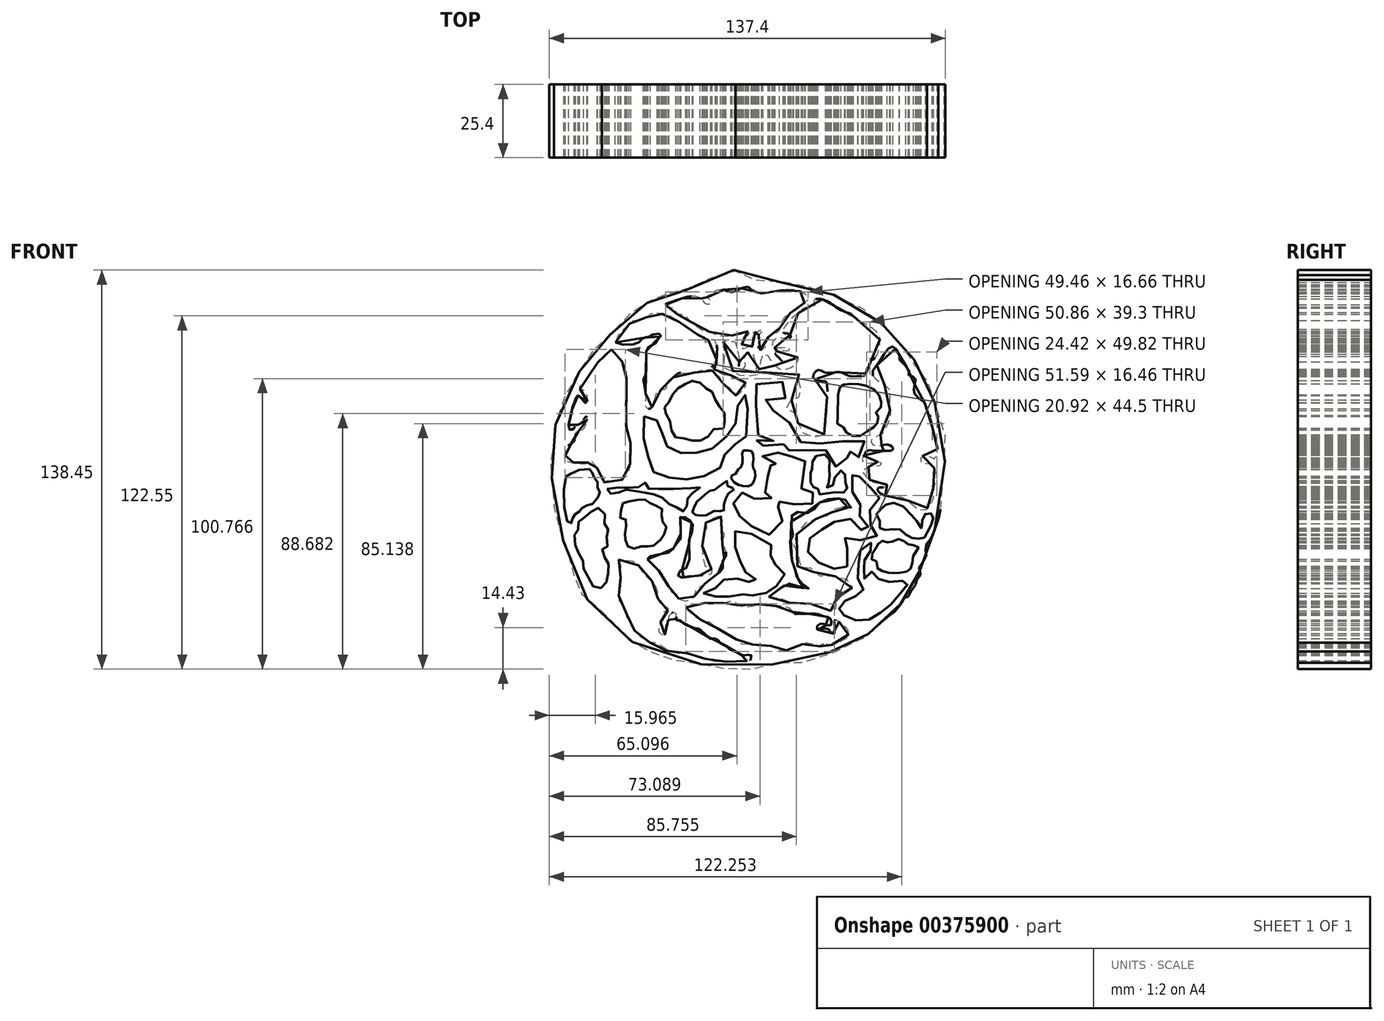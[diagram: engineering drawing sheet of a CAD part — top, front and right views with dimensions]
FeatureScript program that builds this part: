
annotation { "Feature Type Name" : "Feature", "Feature Type Description" : "" }
export const myFeature = defineFeature(function(context is Context, id is Id, definition is map)
    precondition{}
    {
        {
            var Q0;
            Q0=qCreatedBy(makeId("Front.planeOp"),FACE);
            var sketch = newSketch(context, id + "F0", { "sketchPlane" : qUnion([Q0])});
            skFitSpline(sketch, "E0", {"points": [v(-58.3, 41.66) * mm, v(-56.87, 40.83) * mm, v(-56.04, 38.93) * mm, v(-54.73, 37.5) * mm, v(-53.54, 36.31) * mm, v(-53.19, 34.05) * mm, v(-53.07, 31.2) * mm, v(-53.19, 15.04) * mm, v(-52.35, 14.2) * mm, v(-52.23, 11.47) * mm, v(-51.64, 9.21) * mm, v(-51.52, 6.96) * mm, v(-51.64, 3.75) * mm, v(-52.12, 0) * mm, v(-53.07, -2.2) * mm, v(-54.02, -3.38) * mm, v(-56.63, -3.86) * mm, v(-58.65, -3.98) * mm, v(-60.55, -4.45) * mm, v(-61.39, -4.1) * mm, v(-61.86, -2.55) * mm, v(-63.05, 0) * mm, v(-64, 1.6) * mm, v(-64.83, 2.8) * mm, v(-65.55, 3.27) * mm, v(-66.5, 2.44) * mm, v(-67.45, 1.85) * mm, v(-68.64, 1.73) * mm, v(-70.66, 2.08) * mm, v(-71.84, 2.44) * mm, v(-73.4, 2.32) * mm, v(-74.34, 2.56) * mm, v(-74.34, 4.46) * mm, v(-74.34, 6.48) * mm, v(-74.22, 8.03) * mm, v(-73.03, 8.5) * mm, v(-71.49, 9.69) * mm, v(-70.78, 10.88) * mm, v(-70.9, 12.42) * mm, v(-69.7, 13.14) * mm, v(-68.4, 13.73) * mm, v(-67.33, 15.28) * mm, v(-66.85, 16.7) * mm, v(-66.97, 18.37) * mm, v(-67.92, 17.41) * mm, v(-69.23, 15.99) * mm, v(-70.66, 15.04) * mm, v(-71.6, 13.97) * mm, v(-72.68, 13.85) * mm, v(-73.15, 15.28) * mm, v(-72.8, 17.06) * mm, v(-72.44, 18.37) * mm, v(-72.08, 20.15) * mm, v(-71.84, 21.57) * mm, v(-71.13, 23.24) * mm, v(-70.66, 24.66) * mm, v(-69.82, 25.62) * mm, v(-68.75, 24.78) * mm, v(-67.92, 23.6) * mm, v(-66.97, 23.12) * mm, v(-66.62, 25.14) * mm, v(-67.1, 26.57) * mm, v(-67.92, 27.52) * mm, v(-69.23, 28) * mm, v(-69.11, 29.18) * mm, v(-68.04, 30.01) * mm, v(-66.73, 31.68) * mm, v(-65.43, 33.46) * mm, v(-64, 35.48) * mm, v(-63.17, 36.9) * mm, v(-61.86, 38.33) * mm, v(-60.55, 39.76) * mm, v(-58.3, 41.66) * mm]});
            skFitSpline(sketch, "E1", {"points": [v(-56.85, 44.1) * mm, v(-49.42, 43.75) * mm, v(-48.22, 44.83) * mm, v(-46.66, 45.79) * mm, v(-45.1, 46.15) * mm, v(-43.42, 46.99) * mm, v(-41.03, 46.75) * mm, v(-42.23, 45.19) * mm, v(-43.3, 43.5) * mm, v(-44.74, 42.9) * mm, v(-46.06, 41.66) * mm, v(-46.18, 39.76) * mm, v(-46.18, 38.11) * mm, v(-46.18, 35.72) * mm, v(-46.66, 32.24) * mm, v(-47.26, 31.16) * mm, v(-46.9, 29.84) * mm, v(-46.66, 27.8) * mm, v(-46.42, 24.57) * mm, v(-46.42, 21.93) * mm, v(-45.46, 21.09) * mm, v(-44.5, 21.33) * mm, v(-43.66, 22.65) * mm, v(-43.18, 25.05) * mm, v(-42.7, 26.36) * mm, v(-41.27, 27.68) * mm, v(-39.83, 27.92) * mm, v(-38.99, 29) * mm, v(-38.63, 30.68) * mm, v(-36.83, 32) * mm, v(-34.8, 33.46) * mm, v(-31.68, 33.46) * mm, v(-30, 33.46) * mm, v(-27.87, 34.16) * mm, v(-26.86, 34.58) * mm, v(-25.34, 34.75) * mm, v(-23.9, 34.75) * mm, v(-22.55, 33.46) * mm, v(-21.11, 32.38) * mm, v(-20.35, 31.2) * mm, v(-20.18, 30.18) * mm, v(-19, 29.5) * mm, v(-17.56, 28.5) * mm, v(-16.46, 27.31) * mm, v(-16.04, 25.96) * mm, v(-15.2, 25.7) * mm, v(-14.1, 26.21) * mm, v(-12.74, 27.48) * mm, v(-11.9, 28.24) * mm, v(-11.73, 29.68) * mm, v(-12.07, 30.7) * mm, v(-13.67, 31.11) * mm, v(-15.2, 31.28) * mm, v(-16.3, 31.96) * mm, v(-16.89, 32.8) * mm, v(-18.58, 32.64) * mm, v(-20.6, 33.46) * mm, v(-22.1, 34.3) * mm, v(-22.53, 34.69) * mm, v(-23.01, 35.21) * mm, v(-23.45, 35.74) * mm, v(-22.48, 36.08) * mm, v(-21.81, 36.9) * mm, v(-21.86, 37.33) * mm, v(-21.76, 38.83) * mm, v(-22.11, 44.86) * mm, v(-23.16, 44.77) * mm, v(-24.65, 44.86) * mm, v(-25.6, 43.99) * mm, v(-26.05, 44.86) * mm, v(-26.05, 46.35) * mm, v(-27.62, 46.52) * mm, v(-29.28, 47.3) * mm, v(-31.11, 48.88) * mm, v(-33.9, 50.65) * mm, v(-35.06, 51.35) * mm, v(-36.36, 52.18) * mm, v(-37.78, 53.12) * mm, v(-39.31, 53.71) * mm, v(-41.08, 54.07) * mm, v(-42.73, 54.3) * mm, v(-44.74, 54.3) * mm, v(-44.86, 53.24) * mm, v(-46.63, 52.77) * mm, v(-48.04, 52.3) * mm, v(-49.34, 51.7) * mm, v(-50.87, 51.59) * mm, v(-52.4, 50.17) * mm, v(-54.06, 48.76) * mm, v(-55.6, 46.99) * mm, v(-56.85, 44.1) * mm]});
            skFitSpline(sketch, "E2", {"points": [v(-47.03, 18.43) * mm, v(-47.03, 15.19) * mm, v(-47.03, 12.58) * mm, v(-47.03, 9.21) * mm, v(-46.28, 7.85) * mm, v(-45.78, 5.98) * mm, v(-45.66, 3.36) * mm, v(-45.53, 1.12) * mm, v(-44.04, 0) * mm, v(-43.3, -1.5) * mm, v(-41.05, -2.11) * mm, v(-39.68, -2.86) * mm, v(-37.81, -2.86) * mm, v(-35.82, -3.73) * mm, v(-34.33, -3.73) * mm, v(-32.09, -3.36) * mm, v(-30.97, -2.86) * mm, v(-28.23, -2.49) * mm, v(-26.24, -2.24) * mm, v(-24.25, -2.11) * mm, v(-22.38, 0) * mm, v(-20.48, 0.65) * mm, v(-20, 1.6) * mm, v(-19.94, 2.84) * mm, v(-19.58, 4.15) * mm, v(-19, 5.1) * mm, v(-17.68, 6.23) * mm, v(-16.91, 7.18) * mm, v(-16.08, 8.2) * mm, v(-15.3, 8.73) * mm, v(-14.24, 9.62) * mm, v(-12.57, 10.33) * mm, v(-11.68, 11.05) * mm, v(-11.44, 12.17) * mm, v(-11.2, 13) * mm, v(-11.2, 14.25) * mm, v(-11.38, 15.86) * mm, v(-11.15, 16.75) * mm, v(-10.79, 18) * mm, v(-11.03, 18.77) * mm, v(-11.2, 20.61) * mm, v(-10.85, 21.45) * mm, v(-10.73, 23.05) * mm, v(-10.99, 24.42) * mm, v(-11.66, 25.7) * mm, v(-13.01, 25.7) * mm, v(-14.27, 24.8) * mm, v(-14.46, 23.94) * mm, v(-14.46, 22.1) * mm, v(-14.46, 20.37) * mm, v(-15.2, 18.15) * mm, v(-15.2, 16.03) * mm, v(-15.2, 14.17) * mm, v(-16.57, 13.18) * mm, v(-18.02, 11.73) * mm, v(-19.8, 10.27) * mm, v(-21.65, 8.75) * mm, v(-23.24, 7.43) * mm, v(-24.16, 6.7) * mm, v(-26.4, 6.11) * mm, v(-27.93, 5.91) * mm, v(-29.31, 5.85) * mm, v(-30.64, 5.85) * mm, v(-32.22, 5.78) * mm, v(-34, 5.72) * mm, v(-35.39, 5.72) * mm, v(-36.78, 6.44) * mm, v(-38.3, 7.3) * mm, v(-39.35, 8.42) * mm, v(-40.4, 9.68) * mm, v(-40.54, 10.8) * mm, v(-40.54, 11.99) * mm, v(-40.87, 12.91) * mm, v(-41.6, 13.57) * mm, v(-42.39, 15.49) * mm, v(-42.39, 16.68) * mm, v(-43.25, 18.06) * mm, v(-44.7, 18.8) * mm, v(-46.09, 18.6) * mm, v(-47.03, 18.43) * mm]});
            skFitSpline(sketch, "E3", {"points": [v(-39.87, 21.63) * mm, v(-39.75, 19.62) * mm, v(-38.45, 18.56) * mm, v(-37.74, 14.89) * mm, v(-37.14, 12.91) * mm, v(-35.96, 11.1) * mm, v(-33.48, 10.86) * mm, v(-30.64, 10.15) * mm, v(-28.62, 9.8) * mm, v(-25.9, 10.74) * mm, v(-24.25, 12.05) * mm, v(-22.23, 14.3) * mm, v(-19, 14.41) * mm, v(-19, 16.54) * mm, v(-19, 19.15) * mm, v(-20.22, 21.28) * mm, v(-22, 23.17) * mm, v(-22.7, 25.7) * mm, v(-23.65, 27.2) * mm, v(-25.2, 28.02) * mm, v(-26.85, 29.5) * mm, v(-28.98, 30.74) * mm, v(-31.1, 30.5) * mm, v(-33, 29.5) * mm, v(-35.01, 28.38) * mm, v(-36.67, 26.84) * mm, v(-37.85, 24.24) * mm, v(-39.04, 22.58) * mm, v(-39.87, 21.63) * mm]});
            skFitSpline(sketch, "E4", {"points": [v(-74, -2.4) * mm, v(-73.42, -18.32) * mm, v(-72.14, -18.44) * mm, v(-71.67, -16.58) * mm, v(-70.51, -15.18) * mm, v(-69.12, -14.25) * mm, v(-67.84, -12.74) * mm, v(-65.43, -12.16) * mm, v(-64.23, -11.23) * mm, v(-63.17, -9.72) * mm, v(-62.25, -8.2) * mm, v(-63.17, -6.23) * mm, v(-63.17, -4.02) * mm, v(-64.46, -2.62) * mm, v(-65.43, 0) * mm, v(-66.9, 0) * mm, v(-69, 0) * mm, v(-70.98, -0.88) * mm, v(-72.37, -1.46) * mm, v(-74, -2.4) * mm]});
            skFitSpline(sketch, "E5", {"points": [v(-69.78, -18.13) * mm, v(-69.78, -19.14) * mm, v(-69.82, -20.68) * mm, v(-70.4, -21.47) * mm, v(-70.92, -21.82) * mm, v(-71.18, -23.63) * mm, v(-70.96, -25.6) * mm, v(-70.61, -27.46) * mm, v(-69.86, -28.64) * mm, v(-68.97, -30.31) * mm, v(-68.2, -31.53) * mm, v(-67.98, -32.6) * mm, v(-67.98, -34.04) * mm, v(-67.52, -35.41) * mm, v(-66.38, -37.24) * mm, v(-65.43, -39.82) * mm, v(-64.1, -40.81) * mm, v(-63.17, -41.2) * mm, v(-61.44, -40.96) * mm, v(-60.55, -40.05) * mm, v(-59.91, -38.53) * mm, v(-59.61, -36.86) * mm, v(-59.3, -34.65) * mm, v(-59.15, -33.13) * mm, v(-60, -31.99) * mm, v(-60.55, -30.7) * mm, v(-61.2, -29.4) * mm, v(-61.44, -28.18) * mm, v(-61.36, -27.12) * mm, v(-60.55, -26.97) * mm, v(-59.76, -26.74) * mm, v(-59.91, -24.68) * mm, v(-59.91, -23.09) * mm, v(-59.53, -22.02) * mm, v(-59.38, -20.8) * mm, v(-59.84, -19.82) * mm, v(-60.55, -19.28) * mm, v(-60.55, -17.23) * mm, v(-60.55, -15.7) * mm, v(-61.28, -13.96) * mm, v(-63.17, -13.35) * mm, v(-64.33, -13.8) * mm, v(-65.43, -14.8) * mm, v(-66.6, -15.86) * mm, v(-68.05, -16.85) * mm, v(-69.12, -17.69) * mm, v(-69.78, -18.13) * mm]});
            skFitSpline(sketch, "E6", {"points": [v(-59.76, -6.69) * mm, v(-59.76, -8.1) * mm, v(-58.3, -8.44) * mm, v(-57.14, -8.44) * mm, v(-55.39, -7.77) * mm, v(-53.89, -7.02) * mm, v(-52.3, -7.19) * mm, v(-49.89, -7.52) * mm, v(-48.14, -7.94) * mm, v(-45.8, -8.1) * mm, v(-43.64, -8.6) * mm, v(-41.72, -9.1) * mm, v(-40.14, -10.27) * mm, v(-38.63, -11.52) * mm, v(-37.48, -12.69) * mm, v(-35.82, -13.1) * mm, v(-34.33, -13.77) * mm, v(-33.14, -14.52) * mm, v(-32.14, -13.69) * mm, v(-32.14, -12.35) * mm, v(-32.14, -10.85) * mm, v(-31.64, -9.77) * mm, v(-30.64, -8.85) * mm, v(-29.23, -7.27) * mm, v(-27.56, -6.27) * mm, v(-29.64, -6.35) * mm, v(-31.56, -6.6) * mm, v(-40.23, -6.69) * mm, v(-42.56, -6.77) * mm, v(-45.3, -6.69) * mm, v(-45.8, -5.52) * mm, v(-46.56, -4.52) * mm, v(-47.4, -5.69) * mm, v(-49.3, -6.1) * mm, v(-51.64, -6.27) * mm, v(-54.22, -6.27) * mm, v(-56.39, -6.27) * mm, v(-59.76, -6.69) * mm]});
            skFitSpline(sketch, "E7", {"points": [v(-54.38, -11.65) * mm, v(-55.05, -13.87) * mm, v(-55.05, -15.22) * mm, v(-55.18, -16.76) * mm, v(-54.1, -16.76) * mm, v(-53.03, -17.9) * mm, v(-53.03, -19.46) * mm, v(-53.57, -20.53) * mm, v(-53.5, -22.62) * mm, v(-53.43, -23.76) * mm, v(-53.43, -25.38) * mm, v(-52.56, -26.74) * mm, v(-51.35, -27.26) * mm, v(-49.6, -27.4) * mm, v(-48.05, -26.74) * mm, v(-46.9, -26.74) * mm, v(-45.36, -26.74) * mm, v(-44.35, -26.74) * mm, v(-42.33, -25.31) * mm, v(-40.87, -24.03) * mm, v(-40.18, -22.75) * mm, v(-39.5, -21.27) * mm, v(-39.37, -19.46) * mm, v(-40.18, -18.45) * mm, v(-40.87, -17.44) * mm, v(-40.87, -16.1) * mm, v(-40.87, -14.68) * mm, v(-40.87, -13.4) * mm, v(-42.47, -12.73) * mm, v(-43.81, -12.12) * mm, v(-44.89, -11.58) * mm, v(-46.23, -10.5) * mm, v(-47.1, -10.37) * mm, v(-49, -10.5) * mm, v(-51.41, -10.98) * mm, v(-52.76, -11.18) * mm, v(-54.38, -11.65) * mm]});
            skFitSpline(sketch, "E8", {"points": [v(-55.82, -31.21) * mm, v(-55.71, -32.39) * mm, v(-55.07, -33.56) * mm, v(-55.07, -36.33) * mm, v(-55.07, -37.61) * mm, v(-54.97, -39.64) * mm, v(-55.18, -41.35) * mm, v(-55.6, -42.52) * mm, v(-55.82, -44.76) * mm, v(-55.4, -45.93) * mm, v(-54.11, -47.1) * mm, v(-52.94, -50.3) * mm, v(-52.94, -52.33) * mm, v(-51.75, -53.22) * mm, v(-50.69, -55.15) * mm, v(-50.11, -56.2) * mm, v(-48.86, -57.45) * mm, v(-47.13, -58.7) * mm, v(-45.5, -59.76) * mm, v(-43.29, -60.24) * mm, v(-40.87, -60.34) * mm, v(-40.18, -61.88) * mm, v(-38.63, -63.13) * mm, v(-36.85, -63.13) * mm, v(-34.33, -63.8) * mm, v(-31.66, -63.7) * mm, v(-29.73, -64.28) * mm, v(-27.81, -65.05) * mm, v(-26.48, -65.5) * mm, v(-25.25, -65.83) * mm, v(-22.23, -66.56) * mm, v(-20.04, -66.56) * mm, v(-18.33, -66.73) * mm, v(-15.9, -66.56) * mm, v(-13.67, -66.56) * mm, v(-11.66, -66.32) * mm, v(-10.2, -66.32) * mm, v(-9.95, -64.2) * mm, v(-11.9, -64.53) * mm, v(-13.67, -64.12) * mm, v(-15.2, -63.3) * mm, v(-16.95, -62.5) * mm, v(-19, -61.03) * mm, v(-21.02, -59.64) * mm, v(-21.76, -58.75) * mm, v(-24.25, -58.67) * mm, v(-25.17, -57.69) * mm, v(-26.88, -56.22) * mm, v(-28.1, -55.25) * mm, v(-29.49, -54.92) * mm, v(-32.01, -54.1) * mm, v(-33.64, -53.21) * mm, v(-34.33, -52.32) * mm, v(-35.82, -52.23) * mm, v(-35.82, -50.36) * mm, v(-36.9, -49.63) * mm, v(-37.87, -50.04) * mm, v(-38.63, -51.58) * mm, v(-38.63, -53.37) * mm, v(-39.42, -53.86) * mm, v(-39.58, -55.16) * mm, v(-39.5, -56.71) * mm, v(-40.18, -57.44) * mm, v(-41.7, -57.04) * mm, v(-41.7, -55.16) * mm, v(-41.62, -53.62) * mm, v(-40.87, -52.56) * mm, v(-40.18, -51.99) * mm, v(-40.18, -50.69) * mm, v(-40.18, -49.38) * mm, v(-38.63, -48.73) * mm, v(-38.63, -47.6) * mm, v(-40.18, -46.86) * mm, v(-41.54, -46.3) * mm, v(-42.19, -44.58) * mm, v(-42.27, -42.8) * mm, v(-42.68, -41.08) * mm, v(-43.65, -39.45) * mm, v(-45.12, -37.99) * mm, v(-46.83, -36.52) * mm, v(-48.21, -34.32) * mm, v(-49.27, -32.94) * mm, v(-51.06, -31.8) * mm, v(-52.94, -31.72) * mm, v(-55.82, -31.21) * mm]});
            skFitSpline(sketch, "E9", {"points": [v(-45.81, -31.07) * mm, v(-44.91, -32.27) * mm, v(-43.36, -33.53) * mm, v(-42.52, -34.55) * mm, v(-40.87, -35.99) * mm, v(-40.18, -37.79) * mm, v(-38.63, -40.12) * mm, v(-37.84, -42.16) * mm, v(-35.82, -43.42) * mm, v(-35.26, -44.5) * mm, v(-33.7, -45.34) * mm, v(-31.79, -45.46) * mm, v(-30.1, -44.56) * mm, v(-29.33, -43.3) * mm, v(-28.9, -41.62) * mm, v(-27.35, -40.54) * mm, v(-25.13, -38.99) * mm, v(-24.25, -38.09) * mm, v(-22.23, -36.77) * mm, v(-20.7, -35.5) * mm, v(-19.68, -33.9) * mm, v(-19.68, -31.67) * mm, v(-19, -30.65) * mm, v(-18.54, -29.15) * mm, v(-19, -27.18) * mm, v(-19.62, -26.74) * mm, v(-19.62, -24.3) * mm, v(-19, -22.68) * mm, v(-19.62, -21.48) * mm, v(-20.1, -20.64) * mm, v(-20.34, -18.45) * mm, v(-19.74, -17.59) * mm, v(-19.74, -16.57) * mm, v(-20.82, -16.39) * mm, v(-21.76, -16.5) * mm, v(-24.25, -17.53) * mm, v(-25.55, -18.45) * mm, v(-25.31, -20.34) * mm, v(-26.27, -21.84) * mm, v(-26.15, -32.63) * mm, v(-24.95, -34.2) * mm, v(-23.57, -34.6) * mm, v(-23.57, -36.1) * mm, v(-24.25, -36.59) * mm, v(-26.81, -36.65) * mm, v(-29.39, -36.95) * mm, v(-31.07, -36.95) * mm, v(-31.9, -37.3) * mm, v(-34.33, -37.55) * mm, v(-34.9, -37.55) * mm, v(-35.14, -35.69) * mm, v(-34.33, -35.03) * mm, v(-32.75, -34.25) * mm, v(-31.43, -33.17) * mm, v(-31.07, -22.08) * mm, v(-30.17, -21.42) * mm, v(-30.17, -18.96) * mm, v(-31, -17.77) * mm, v(-31.9, -16.93) * mm, v(-33.05, -16.39) * mm, v(-34.33, -16.33) * mm, v(-34.33, -18.45) * mm, v(-34.33, -19.74) * mm, v(-34.33, -21.24) * mm, v(-34.33, -24.18) * mm, v(-35.14, -24.96) * mm, v(-36.4, -26.74) * mm, v(-37.36, -28.14) * mm, v(-38.63, -28.92) * mm, v(-40.18, -29.1) * mm, v(-40.87, -29.27) * mm, v(-42.82, -29.7) * mm, v(-44.8, -30.05) * mm, v(-45.51, -30.35) * mm, v(-45.81, -31.07) * mm]});
            skFitSpline(sketch, "E10", {"points": [v(-32.56, -47.89) * mm, v(-30.67, -49.78) * mm, v(-28.67, -51.47) * mm, v(-25.93, -52.52) * mm, v(-24.25, -52.94) * mm, v(-21.76, -54.94) * mm, v(-19, -56.71) * mm, v(-15.2, -58.73) * mm, v(-13.67, -60.3) * mm, v(-10.77, -60.52) * mm, v(-9.2, -60.73) * mm, v(-6.25, -61.05) * mm, v(-3.82, -61.05) * mm, v(-1.61, -61.78) * mm, v(0, -62.62) * mm, v(1.97, -63.05) * mm, v(3.44, -61.68) * mm, v(5.65, -61.89) * mm, v(8.5, -60.3) * mm, v(11.13, -60.3) * mm, v(13.02, -61.15) * mm, v(14.81, -61.15) * mm, v(15.13, -60.1) * mm, v(16.7, -60.94) * mm, v(18.92, -60.52) * mm, v(22.07, -59.15) * mm, v(23.86, -57.47) * mm, v(23.55, -55.36) * mm, v(22.18, -54.2) * mm, v(20.6, -52.83) * mm, v(19.13, -52.3) * mm, v(19.13, -56.71) * mm, v(18.18, -56.71) * mm, v(16.5, -55.15) * mm, v(14.7, -55.36) * mm, v(13.02, -55.47) * mm, v(13.34, -53.89) * mm, v(14.92, -53.47) * mm, v(16.28, -54) * mm, v(17.86, -53.89) * mm, v(17.86, -52.1) * mm, v(17.23, -51.36) * mm, v(15.02, -50.83) * mm, v(11.97, -49.89) * mm, v(9.13, -50.1) * mm, v(6.6, -50.1) * mm, v(5.23, -50.1) * mm, v(3.97, -48.52) * mm, v(2.28, -47.68) * mm, v(-0.88, -47.36) * mm, v(-2.14, -47.36) * mm, v(-4.98, -46.41) * mm, v(-7.72, -46.94) * mm, v(-10.14, -47.68) * mm, v(-13.67, -47.36) * mm, v(-15.2, -46.1) * mm, v(-17.5, -45.89) * mm, v(-19, -46.3) * mm, v(-21.76, -46.3) * mm, v(-24.25, -46.3) * mm, v(-27.2, -46.52) * mm, v(-29.83, -46.94) * mm, v(-32.56, -47.89) * mm]});
            skFitSpline(sketch, "E11", {"points": [v(-26.42, -42.99) * mm, v(-24.25, -42) * mm, v(-22.23, -41.03) * mm, v(-22.23, -40.05) * mm, v(-19, -38.1) * mm, v(-17.12, -37.97) * mm, v(-13.67, -37.85) * mm, v(-11.86, -38.34) * mm, v(-10.14, -39.2) * mm, v(-7.7, -39.32) * mm, v(-8.92, -37.48) * mm, v(-10.14, -36.75) * mm, v(-12.23, -35.28) * mm, v(-13.67, -33.93) * mm, v(-13.67, -30.65) * mm, v(-15.2, -27.7) * mm, v(-15.2, -23.66) * mm, v(-15.2, -21.09) * mm, v(-13.67, -20.35) * mm, v(-13.67, -21.58) * mm, v(-11.74, -22.31) * mm, v(-10.14, -22.31) * mm, v(-8.07, -22.92) * mm, v(-6.72, -23.9) * mm, v(-5, -24.88) * mm, v(-4.03, -25.25) * mm, v(-2.44, -26.74) * mm, v(-2.2, -28.18) * mm, v(-3.3, -30.65) * mm, v(-2.68, -31.98) * mm, v(-1.34, -33.08) * mm, v(0.86, -34.67) * mm, v(1.72, -36.87) * mm, v(0, -39.56) * mm, v(-1.95, -40.9) * mm, v(-3.42, -42) * mm, v(-6.6, -43.6) * mm, v(-9.17, -43.72) * mm, v(-10.14, -43.72) * mm, v(-11.62, -42.99) * mm, v(-13.67, -43.72) * mm, v(-16.5, -44.09) * mm, v(-19, -44.09) * mm, v(-21.76, -44.09) * mm, v(-24.25, -44.09) * mm, v(-26.42, -42.99) * mm]});
            skFitSpline(sketch, "E12", {"points": [v(-3.65, -44.25) * mm, v(-1.62, -42.43) * mm, v(0, -41.52) * mm, v(1.1, -40.6) * mm, v(2.63, -39.7) * mm, v(4.65, -39.8) * mm, v(7.59, -40.91) * mm, v(10.22, -41.22) * mm, v(8.2, -39.9) * mm, v(6.68, -38.38) * mm, v(5.77, -36.66) * mm, v(5.26, -34.53) * mm, v(4.55, -32.3) * mm, v(4.05, -29.78) * mm, v(3.84, -27.35) * mm, v(3.84, -24.2) * mm, v(4.65, -23.6) * mm, v(4.45, -21.98) * mm, v(4.25, -20.26) * mm, v(4.25, -16.1) * mm, v(5.46, -14.59) * mm, v(7.59, -15.2) * mm, v(10.02, -15) * mm, v(12.25, -13.58) * mm, v(13.36, -12.16) * mm, v(14.58, -11.04) * mm, v(17.41, -10.23) * mm, v(19.64, -10.03) * mm, v(21.66, -10.13) * mm, v(23.59, -11.15) * mm, v(24.8, -13.17) * mm, v(23.69, -13.17) * mm, v(20.55, -13.17) * mm, v(19.23, -13.47) * mm, v(18.63, -14.28) * mm, v(17.1, -15.6) * mm, v(15.39, -16.61) * mm, v(13.66, -16.92) * mm, v(11.74, -17.42) * mm, v(8.4, -19.04) * mm, v(6.17, -22.08) * mm, v(5.16, -24.2) * mm, v(4.96, -26.74) * mm, v(6.07, -29.37) * mm, v(7.29, -30.38) * mm, v(7.7, -31.9) * mm, v(5.87, -33.02) * mm, v(6.98, -33.83) * mm, v(8.9, -33.62) * mm, v(10.63, -33.93) * mm, v(12.15, -35.85) * mm, v(14.47, -36.86) * mm, v(17.92, -36.86) * mm, v(21.36, -37.57) * mm, v(24.5, -38.69) * mm, v(25.2, -40.5) * mm, v(24.2, -42.23) * mm, v(22.78, -42.94) * mm, v(20.75, -43.55) * mm, v(19.44, -45.67) * mm, v(19.33, -47.2) * mm, v(19.33, -48.5) * mm, v(17.82, -49.01) * mm, v(17.41, -49.01) * mm, v(14.88, -47.8) * mm, v(11.94, -46.68) * mm, v(9.2, -46.68) * mm, v(6.88, -46.38) * mm, v(4.05, -46.38) * mm, v(1.72, -45.17) * mm, v(0, -44.96) * mm, v(-3.65, -44.25) * mm]});
            skFitSpline(sketch, "E13", {"points": [v(22.77, -45.6) * mm, v(21.94, -47.02) * mm, v(20.95, -47.51) * mm, v(20.62, -49.26) * mm, v(20.7, -50.5) * mm, v(22.52, -50.5) * mm, v(24.27, -51.66) * mm, v(26.84, -52.4) * mm, v(29.5, -52.74) * mm, v(31.23, -52) * mm, v(33.64, -50.67) * mm, v(35.38, -49.42) * mm, v(37.2, -48.43) * mm, v(38.78, -46.68) * mm, v(40.36, -45.44) * mm, v(41.69, -43.2) * mm, v(43.35, -41.7) * mm, v(44.42, -39.8) * mm, v(44.6, -38.3) * mm, v(43.35, -38.39) * mm, v(41.69, -39.05) * mm, v(39.12, -39.14) * mm, v(36.7, -38.8) * mm, v(35.38, -38.55) * mm, v(33.97, -37.64) * mm, v(32.98, -36.56) * mm, v(32.31, -35.73) * mm, v(31.15, -35.24) * mm, v(29.82, -36.65) * mm, v(29.33, -37.9) * mm, v(28.58, -36.48) * mm, v(29.33, -34.4) * mm, v(30.07, -33.9) * mm, v(29.33, -32.5) * mm, v(29.58, -31.17) * mm, v(30.32, -29.6) * mm, v(31.57, -28.27) * mm, v(32.31, -26.6) * mm, v(32.31, -25.36) * mm, v(30.49, -26.2) * mm, v(28.75, -27.52) * mm, v(27.75, -28.52) * mm, v(27.42, -31.67) * mm, v(27.34, -34.08) * mm, v(27.17, -36.73) * mm, v(27.25, -38.72) * mm, v(28.41, -40.46) * mm, v(29.08, -42.62) * mm, v(27.58, -43.28) * mm, v(26, -44.11) * mm, v(24.35, -44.36) * mm, v(22.77, -45.6) * mm]});
            skFitSpline(sketch, "E14", {"points": [v(39.53, -35.88) * mm, v(41.54, -35.8) * mm, v(43.86, -35.5) * mm, v(44.87, -34.96) * mm, v(45.88, -33.64) * mm, v(46.18, -31.55) * mm, v(46.57, -29.54) * mm, v(47.42, -28.38) * mm, v(48.04, -27.52) * mm, v(48.04, -26.36) * mm, v(45.41, -26.36) * mm, v(44.25, -25.67) * mm, v(43.01, -24.82) * mm, v(41.93, -24.2) * mm, v(39.68, -24.66) * mm, v(38.37, -25.43) * mm, v(36.97, -25.05) * mm, v(35.66, -24.74) * mm, v(34.5, -25.51) * mm, v(33.8, -26.44) * mm, v(32.8, -28.3) * mm, v(32.18, -29.15) * mm, v(31.94, -31.09) * mm, v(33.34, -31.47) * mm, v(33.88, -33.8) * mm, v(34.5, -34.96) * mm, v(36.59, -35.34) * mm, v(38.29, -35.96) * mm, v(39.53, -35.88) * mm]});
            skFitSpline(sketch, "E15", {"points": [v(23.5, -33.69) * mm, v(22.07, -34.26) * mm, v(20.17, -34.45) * mm, v(19.12, -34.45) * mm, v(17.22, -34.35) * mm, v(14.56, -32.55) * mm, v(12.94, -32.17) * mm, v(10.76, -30.84) * mm, v(10.19, -29.03) * mm, v(9.05, -27.04) * mm, v(9.43, -25.42) * mm, v(10.66, -23.71) * mm, v(11.8, -22) * mm, v(13.04, -20.86) * mm, v(15.98, -20.67) * mm, v(17.22, -19.53) * mm, v(18.27, -18.86) * mm, v(20.36, -17.25) * mm, v(21.36, -17.25) * mm, v(24.63, -17.15) * mm, v(26.25, -17.82) * mm, v(27.3, -19.53) * mm, v(28.62, -21.15) * mm, v(29.29, -21.15) * mm, v(30.9, -21.15) * mm, v(31, -20) * mm, v(29.57, -19.63) * mm, v(28.34, -18.3) * mm, v(27.86, -16.2) * mm, v(27.3, -15.25) * mm, v(28.43, -14.02) * mm, v(28.24, -12.5) * mm, v(27.39, -11.07) * mm, v(26.44, -9.65) * mm, v(25.3, -7.56) * mm, v(25.68, -4.7) * mm, v(25.4, -2.9) * mm, v(25.4, -0.9) * mm, v(26.06, 0) * mm, v(27.2, -1.67) * mm, v(28.34, -3.47) * mm, v(29.67, -4.7) * mm, v(31.95, -6.6) * mm, v(33.37, -7.84) * mm, v(34.42, -9.08) * mm, v(34.7, -9.84) * mm, v(33.18, -10.7) * mm, v(31.85, -12.5) * mm, v(31.19, -14.68) * mm, v(31.19, -16.77) * mm, v(31.28, -18.58) * mm, v(32.04, -20.2) * mm, v(32.8, -21.24) * mm, v(33.85, -22.29) * mm, v(33.56, -23.24) * mm, v(31.1, -23.9) * mm, v(28.62, -24.47) * mm, v(25.49, -24.76) * mm, v(23.97, -24.38) * mm, v(22.64, -23.8) * mm, v(21.36, -25.33) * mm, v(22.64, -26.66) * mm, v(23.78, -27.9) * mm, v(24.06, -30.46) * mm, v(23.5, -33.69) * mm]});
            skFitSpline(sketch, "E16", {"points": [v(49.22, -20.4) * mm, v(49.58, -17.6) * mm, v(50.3, -15.54) * mm, v(51.76, -15.42) * mm, v(53.1, -15.3) * mm, v(53.34, -17.12) * mm, v(52.61, -19.3) * mm, v(51.64, -21.12) * mm, v(50.55, -23.18) * mm, v(49.58, -23.91) * mm, v(47.64, -23.91) * mm, v(45.94, -23.8) * mm, v(43.76, -22.58) * mm, v(42.18, -20.88) * mm, v(40.48, -20.76) * mm, v(37.82, -20.76) * mm, v(35.4, -21) * mm, v(34.78, -19.9) * mm, v(34.78, -17.85) * mm, v(33.7, -15.42) * mm, v(35.03, -13.85) * mm, v(36.36, -12.51) * mm, v(38.06, -11.9) * mm, v(41.58, -11.9) * mm, v(46.06, -16.15) * mm, v(47.52, -17.73) * mm, v(49.22, -20.4) * mm]});
            skFitSpline(sketch, "E17", {"points": [v(-22.67, -7.13) * mm, v(-23.77, -7.25) * mm, v(-25.6, -8.47) * mm, v(-27.06, -9.81) * mm, v(-28.53, -11.03) * mm, v(-29.75, -13.36) * mm, v(-30.12, -15.07) * mm, v(-29.02, -15.8) * mm, v(-27.3, -16.04) * mm, v(-25.23, -15.8) * mm, v(-24.38, -15.31) * mm, v(-22.79, -14.46) * mm, v(-20.83, -14.46) * mm, v(-19.37, -14.33) * mm, v(-19.37, -12.62) * mm, v(-18.64, -10.06) * mm, v(-17.66, -8.23) * mm, v(-15.58, -6.76) * mm, v(-16.31, -6.4) * mm, v(-18.02, -5.66) * mm, v(-18.27, -3.95) * mm, v(-19.61, -4.93) * mm, v(-20.83, -5.78) * mm, v(-22.67, -7.13) * mm]});
            skFitSpline(sketch, "E18", {"points": [v(-10.94, 6.56) * mm, v(-9.6, 6.31) * mm, v(-9.1, 4.97) * mm, v(-9.1, 2.65) * mm, v(-9.23, 1.06) * mm, v(-8.74, 0) * mm, v(-8.37, -2.24) * mm, v(-8.86, -4.07) * mm, v(-10.2, -5.66) * mm, v(-12.4, -5.78) * mm, v(-14.48, -5.17) * mm, v(-16.31, -3.83) * mm, v(-16.8, -2.24) * mm, v(-15.46, -1.75) * mm, v(-14.36, 0) * mm, v(-13.14, 1.18) * mm, v(-12.9, 3.14) * mm, v(-12.9, 5.1) * mm, v(-12.77, 6.43) * mm, v(-10.94, 6.56) * mm]});
            skFitSpline(sketch, "E19", {"points": [v(-13.02, -7.98) * mm, v(-14.73, -8.47) * mm, v(-15.58, -10.67) * mm, v(-16.31, -12.62) * mm, v(-16.07, -14.46) * mm, v(-13.87, -16.04) * mm, v(-12.4, -17.75) * mm, v(-11.06, -18.85) * mm, v(-8.86, -20.2) * mm, v(-5.69, -21.66) * mm, v(-2.88, -22.76) * mm, v(0, -22.15) * mm, v(1.15, -14.7) * mm, v(1.15, -13.11) * mm, v(0, -12.99) * mm, v(-2.39, -12.13) * mm, v(-1.41, -11.16) * mm, v(0, -11.16) * mm, v(2.38, -11.28) * mm, v(3.72, -11.77) * mm, v(5.92, -12.13) * mm, v(9.46, -12.74) * mm, v(11.66, -11.52) * mm, v(12.64, -9.57) * mm, v(11.54, -9.57) * mm, v(11.54, -7.13) * mm, v(9.58, -7.13) * mm, v(7.87, -7.13) * mm, v(7.87, -5.78) * mm, v(8.73, -5.17) * mm, v(8.36, -2.48) * mm, v(8.12, 0) * mm, v(8.24, 2.04) * mm, v(8.85, 2.65) * mm, v(8.6, 3.87) * mm, v(6.28, 3.87) * mm, v(4.09, 4.72) * mm, v(2, 5.95) * mm, v(0, 5.95) * mm, v(-1.66, 5.7) * mm, v(-6.05, 5.7) * mm, v(-5.2, 3.38) * mm, v(-4.59, 2.77) * mm, v(-2.39, 2.9) * mm, v(0, 0) * mm, v(-2.02, 1.18) * mm, v(-3.37, 1.43) * mm, v(-3.85, 1.3) * mm, v(-3.85, 0) * mm, v(-4.1, -2.48) * mm, v(-6.18, -5.42) * mm, v(-5.2, -7.86) * mm, v(-3.12, -8.6) * mm, v(-1.53, -9.7) * mm, v(-3.24, -9.94) * mm, v(-5.44, -10.06) * mm, v(-8.13, -10.18) * mm, v(-9.96, -10.18) * mm, v(-11.67, -9.2) * mm, v(-13.02, -7.98) * mm]});
            skFitSpline(sketch, "E20", {"points": [v(10.8, -4.51) * mm, v(10.9, -2.26) * mm, v(10.72, 0.77) * mm, v(11.41, 0) * mm, v(11.5, 2.06) * mm, v(11.76, 3.97) * mm, v(13.14, 4.83) * mm, v(15.39, 5.18) * mm, v(16.86, 4.74) * mm, v(17.38, 2.15) * mm, v(17.2, 0) * mm, v(17.38, -1.14) * mm, v(17.47, -2.95) * mm, v(17.2, -4.77) * mm, v(16, -5.2) * mm, v(16.43, -6.15) * mm, v(17.98, -6.15) * mm, v(18.68, -4.86) * mm, v(19.2, -2.95) * mm, v(19.71, -1.66) * mm, v(22.57, 0) * mm, v(22.66, -2.35) * mm, v(22.74, -4.17) * mm, v(23.17, -4.94) * mm, v(23.43, -6.07) * mm, v(23.6, -7.13) * mm, v(22.4, -7.97) * mm, v(20.32, -7.8) * mm, v(18.16, -8.14) * mm, v(16.6, -8.23) * mm, v(14.78, -8.32) * mm, v(13.4, -8.58) * mm, v(13.31, -7.13) * mm, v(13.23, -6.07) * mm, v(12.1, -6.07) * mm, v(11.06, -5.9) * mm, v(10.8, -4.51) * mm]});
            skPoint(sketch, "E21.13.internal.snap0", {"position": v(64.71, -3) * mm});
            skPoint(sketch, "E21.78.internal.snap0", {"position": v(64.71, -3) * mm});
            skFitSpline(sketch, "E21", {"points": [v(36.68, -9.04) * mm, v(38.29, -8.92) * mm, v(41.69, -9.29) * mm, v(43.76, -10.26) * mm, v(45.23, -11.28) * mm, v(47.06, -13.07) * mm, v(48.65, -14.17) * mm, v(50.85, -13.93) * mm, v(52.8, -11.28) * mm, v(53.29, -11.28) * mm, v(53.41, -8.92) * mm, v(53.29, -7.13) * mm, v(54.02, -4.89) * mm, v(54.76, -3) * mm, v(54.51, -1.75) * mm, v(53.9, 0) * mm, v(52.43, 1.95) * mm, v(49.26, 2.2) * mm, v(48.77, 3.42) * mm, v(49.75, 4.72) * mm, v(51.58, 4.72) * mm, v(53.78, 3.66) * mm, v(54.63, 4.72) * mm, v(54.63, 7.94) * mm, v(53.53, 9.28) * mm, v(53.05, 10.63) * mm, v(53.05, 13.07) * mm, v(53.05, 16.12) * mm, v(52.68, 18.08) * mm, v(51.82, 18.81) * mm, v(50.36, 23.09) * mm, v(49.5, 23.82) * mm, v(46.82, 26.39) * mm, v(46.57, 27.85) * mm, v(47.08, 30.41) * mm, v(46.93, 32) * mm, v(44.9, 32.59) * mm, v(45.05, 34.18) * mm, v(43.76, 35.92) * mm, v(43.76, 36.06) * mm, v(41.69, 37.94) * mm, v(41.69, 39.54) * mm, v(39.84, 42.3) * mm, v(38.29, 42.44) * mm, v(35.64, 38.96) * mm, v(33.6, 36.06) * mm, v(32.16, 33.3) * mm, v(33.46, 31.28) * mm, v(36.07, 29.54) * mm, v(38.29, 27.52) * mm, v(38.29, 26.07) * mm, v(38.29, 21.58) * mm, v(38.29, 17.81) * mm, v(36.5, 14.04) * mm, v(35.92, 12.74) * mm, v(33.75, 11.44) * mm, v(31.72, 10.13) * mm, v(32.74, 8.4) * mm, v(35.5, 8.4) * mm, v(38.29, 8.4) * mm, v(39.4, 7.1) * mm, v(38.29, 6.51) * mm, v(35.78, 6.51) * mm, v(34.33, 6.51) * mm, v(32.74, 6.51) * mm, v(30.57, 6.51) * mm, v(28.68, 3.32) * mm, v(29.4, 2.02) * mm, v(30.71, 2.31) * mm, v(33.17, 2.31) * mm, v(34.77, 2.75) * mm, v(35.35, 1.73) * mm, v(33.67, 1.15) * mm, v(31.79, 1.15) * mm, v(31.02, 0.98) * mm, v(29.57, 0) * mm, v(28.71, 0) * mm, v(29.4, -1.75) * mm, v(30.85, -3) * mm, v(31.96, -4.23) * mm, v(33.58, -4.65) * mm, v(34.86, -4.57) * mm, v(36.4, -4.57) * mm, v(37.34, -5.5) * mm, v(35.97, -6.2) * mm, v(34.6, -6.28) * mm, v(34, -7.13) * mm, v(36.68, -9.04) * mm]});
            skFitSpline(sketch, "E22", {"points": [v(-7.95, 10.1) * mm, v(-6.86, 9.76) * mm, v(-5.42, 9.42) * mm, v(-4.4, 9.42) * mm, v(-2.14, 9.5) * mm, v(-2.14, 9.97) * mm, v(-3.58, 9.97) * mm, v(-4.53, 10.04) * mm, v(-5.5, 10.31) * mm, v(-6.72, 11.06) * mm, v(-7.4, 11.88) * mm, v(-7.75, 14.62) * mm, v(-7.54, 15.99) * mm, v(-8.02, 21.45) * mm, v(-8.5, 23.85) * mm, v(-8.5, 24.6) * mm, v(-8.64, 28.02) * mm, v(-8.43, 29.18) * mm, v(-5.97, 30.68) * mm, v(-2.76, 30.82) * mm, v(-0.57, 30.55) * mm, v(1.96, 30) * mm, v(3.2, 28.36) * mm, v(4.01, 26.65) * mm, v(2.85, 25.56) * mm, v(1.34, 24.19) * mm, v(0, 23.64) * mm, v(-2.55, 23.3) * mm, v(-3.44, 23.57) * mm, v(-4.94, 24.12) * mm, v(-5.56, 22.82) * mm, v(-6.1, 21.18) * mm, v(-4.74, 20.5) * mm, v(-1.87, 20.5) * mm, v(-0.91, 20.22) * mm, v(0.6, 19.34) * mm, v(2.58, 17.35) * mm, v(3.26, 16.53) * mm, v(4.35, 14.76) * mm, v(4.83, 13.93) * mm, v(6, 11.95) * mm, v(7.16, 9.76) * mm, v(8.66, 8.88) * mm, v(10.23, 8.26) * mm, v(12, 8.88) * mm, v(13.3, 9.01) * mm, v(15.5, 9.08) * mm, v(17.82, 9.42) * mm, v(19.19, 10.38) * mm, v(21.58, 9.9) * mm, v(23.08, 9.08) * mm, v(25.54, 9.5) * mm, v(28.42, 9.9) * mm, v(29.17, 9.9) * mm, v(30.8, 8.6) * mm, v(29.92, 7.78) * mm, v(28.62, 6.14) * mm, v(27.6, 4.98) * mm, v(26.84, 2.18) * mm, v(25, 1.9) * mm, v(25, 3) * mm, v(24.59, 6.14) * mm, v(24.66, 7.99) * mm, v(23.08, 7.1) * mm, v(23.08, 5.6) * mm, v(23.29, 4.3) * mm, v(23.5, 3.4) * mm, v(23.43, 1.9) * mm, v(22.33, 1.22) * mm, v(21.44, 1.22) * mm, v(20.08, 1.22) * mm, v(19.12, 1.15) * mm, v(18.91, 4.57) * mm, v(18.37, 6) * mm, v(16.66, 6.21) * mm, v(15.77, 7.1) * mm, v(14.13, 7.1) * mm, v(12.21, 6.9) * mm, v(11.53, 6.83) * mm, v(9.27, 6.69) * mm, v(7.84, 7.03) * mm, v(6.27, 7.37) * mm, v(5.65, 6.21) * mm, v(3.94, 6.28) * mm, v(2.99, 7.3) * mm, v(3.6, 8.8) * mm, v(3.67, 10.31) * mm, v(2.17, 9.63) * mm, v(1.2, 8.6) * mm, v(0, 8.26) * mm, v(-1.18, 8.26) * mm, v(-3.58, 8.12) * mm, v(-5.22, 8.2) * mm, v(-7.47, 8.33) * mm, v(-8.98, 8.33) * mm, v(-9.52, 9.15) * mm, v(-8.84, 9.97) * mm, v(-7.95, 10.1) * mm]});
            skFitSpline(sketch, "E23", {"points": [v(-39.5, 57.14) * mm, v(-38.67, 56.06) * mm, v(-37.68, 56.4) * mm, v(-36.44, 55.65) * mm, v(-35.62, 53.92) * mm, v(-33.72, 53.84) * mm, v(-31.82, 52.27) * mm, v(-30.59, 51.11) * mm, v(-28.69, 49.63) * mm, v(-25.64, 47.9) * mm, v(-24.32, 47.82) * mm, v(-22.26, 46.9) * mm, v(-18.54, 46.25) * mm, v(-15.99, 46.66) * mm, v(-14.42, 46.9) * mm, v(-12.52, 47.32) * mm, v(-11.45, 48.06) * mm, v(-10.7, 47.07) * mm, v(-12.03, 46.33) * mm, v(-12.6, 45.34) * mm, v(-13.02, 43.7) * mm, v(-12.94, 42.04) * mm, v(-12.11, 42.04) * mm, v(-10.87, 42.7) * mm, v(-10.05, 42.7) * mm, v(-8.98, 42.78) * mm, v(-9.14, 44.68) * mm, v(-9.22, 47.65) * mm, v(-8.15, 47.65) * mm, v(-6.42, 48.48) * mm, v(-5.68, 48.64) * mm, v(-6.09, 47.9) * mm, v(-7.24, 46.66) * mm, v(-7.4, 44.68) * mm, v(-7.16, 43.03) * mm, v(-7.16, 41.63) * mm, v(-6.42, 41.46) * mm, v(-5.18, 42.12) * mm, v(-4.6, 43.7) * mm, v(-4.11, 45.26) * mm, v(-3.2, 46.74) * mm, v(-2.21, 46.9) * mm, v(0, 48.31) * mm, v(0, 48.89) * mm, v(0.6, 49.88) * mm, v(0.92, 51.77) * mm, v(2.4, 53.34) * mm, v(4.47, 54.74) * mm, v(5.79, 55.49) * mm, v(7.27, 56.64) * mm, v(8.6, 57.71) * mm, v(9.91, 59.03) * mm, v(9.75, 59.94) * mm, v(8.5, 61.01) * mm, v(6.78, 62.08) * mm, v(5.54, 62.41) * mm, v(4.06, 62.41) * mm, v(1.42, 62.25) * mm, v(-1.06, 62) * mm, v(-3.37, 61.1) * mm, v(-6.42, 61.18) * mm, v(-9.55, 62.25) * mm, v(-11.04, 63.32) * mm, v(-14.34, 62.33) * mm, v(-15.74, 61.67) * mm, v(-18.3, 61.92) * mm, v(-19.29, 62.41) * mm, v(-22.59, 61.75) * mm, v(-23.99, 60.6) * mm, v(-25.06, 60.02) * mm, v(-23.82, 58.13) * mm, v(-25.06, 57.22) * mm, v(-26.54, 58.62) * mm, v(-27.86, 59.7) * mm, v(-30.1, 60.1) * mm, v(-32.4, 59.77) * mm, v(-34.46, 59.11) * mm, v(-36.94, 58.37) * mm, v(-38.83, 57.71) * mm, v(-39.5, 57.14) * mm]});
            skFitSpline(sketch, "E24", {"points": [v(-19.54, 44.28) * mm, v(-19.2, 39.8) * mm, v(-19.2, 37.22) * mm, v(-19.2, 34.38) * mm, v(-17.22, 34.38) * mm, v(-14.78, 33.39) * mm, v(-13.6, 32.73) * mm, v(-11.48, 32.53) * mm, v(-9.37, 32.46) * mm, v(-5.4, 33.45) * mm, v(-2.37, 33.59) * mm, v(0, 33) * mm, v(2.65, 33.26) * mm, v(5.03, 33.39) * mm, v(6.75, 33) * mm, v(6.28, 31.67) * mm, v(6.75, 29.03) * mm, v(7.67, 26.85) * mm, v(6.42, 24.87) * mm, v(4.37, 24.08) * mm, v(3.18, 23.15) * mm, v(2, 21.44) * mm, v(3.77, 20.97) * mm, v(5.1, 19.78) * mm, v(6.02, 16.88) * mm, v(7.6, 14.37) * mm, v(8.33, 12.52) * mm, v(10.58, 11.13) * mm, v(14.34, 12.06) * mm, v(15.33, 12) * mm, v(16.12, 14.83) * mm, v(16.25, 19.06) * mm, v(16.72, 22.23) * mm, v(16.52, 24.54) * mm, v(16.52, 25.46) * mm, v(16.65, 27.05) * mm, v(16.65, 27.38) * mm, v(16.52, 29.62) * mm, v(16.12, 30.55) * mm, v(14.27, 30.81) * mm, v(12.42, 31.2) * mm, v(11.63, 32) * mm, v(12.5, 34.05) * mm, v(13.74, 34.5) * mm, v(15.92, 33.65) * mm, v(18.37, 33.59) * mm, v(20.67, 33.78) * mm, v(22.03, 33.5) * mm, v(23.78, 32.52) * mm, v(26.5, 32.33) * mm, v(29.7, 32.62) * mm, v(30, 33.69) * mm, v(30.67, 36.4) * mm, v(33.68, 39.42) * mm, v(34.75, 43.6) * mm, v(34.85, 44.95) * mm, v(34.36, 46.8) * mm, v(32.23, 48.93) * mm, v(30.41, 50.15) * mm, v(27.66, 51.46) * mm, v(24.8, 53.85) * mm, v(22.64, 54.69) * mm, v(19.9, 56.12) * mm, v(17.5, 57.8) * mm, v(15.11, 59) * mm, v(13.44, 59.23) * mm, v(12, 58.87) * mm, v(12.12, 56.72) * mm, v(8.9, 56.12) * mm, v(6.74, 54.45) * mm, v(3.87, 52.18) * mm, v(2.92, 50.98) * mm, v(1.36, 48.6) * mm, v(1.48, 47.4) * mm, v(3.28, 47.04) * mm, v(3.87, 45.84) * mm, v(1.96, 45.48) * mm, v(0, 45.6) * mm, v(-1.39, 45.25) * mm, v(-2.58, 43.81) * mm, v(-1.74, 42.3) * mm, v(0, 42.3) * mm, v(1.36, 42.3) * mm, v(3.16, 42.3) * mm, v(3.16, 41.18) * mm, v(1.6, 41.18) * mm, v(-1.27, 40.82) * mm, v(-1.5, 40.22) * mm, v(0, 38.55) * mm, v(1.36, 37.36) * mm, v(3.76, 38.07) * mm, v(6.03, 39.15) * mm, v(6.27, 36.88) * mm, v(4.47, 35.56) * mm, v(2.56, 34.73) * mm, v(0, 34.6) * mm, v(0, 34.85) * mm, v(-2.34, 36.64) * mm, v(-3.18, 38.43) * mm, v(-4.13, 39.63) * mm, v(-6.05, 39.75) * mm, v(-6.64, 36.28) * mm, v(-7.12, 34.6) * mm, v(-7.96, 33.89) * mm, v(-8.08, 35.56) * mm, v(-8.32, 37.36) * mm, v(-9.04, 39.75) * mm, v(-9.75, 40.7) * mm, v(-11.67, 40.22) * mm, v(-12.38, 38.31) * mm, v(-11.9, 36.52) * mm, v(-12.5, 34.49) * mm, v(-13.94, 35.08) * mm, v(-13.94, 37.36) * mm, v(-14.18, 40.22) * mm, v(-14.77, 42.3) * mm, v(-15.37, 44.17) * mm, v(-17.76, 44.17) * mm, v(-19.54, 44.28) * mm]});
            skFitSpline(sketch, "E25", {"points": [v(21, 28.57) * mm, v(20.27, 25.54) * mm, v(20.36, 23.98) * mm, v(20.18, 20.13) * mm, v(20.18, 18.57) * mm, v(20.18, 15.72) * mm, v(22.02, 14.8) * mm, v(23.12, 13.06) * mm, v(24.59, 11.87) * mm, v(27.98, 11.6) * mm, v(30.46, 13.34) * mm, v(33.12, 14.9) * mm, v(33.76, 15.81) * mm, v(34.5, 17.74) * mm, v(33.4, 19.3) * mm, v(33.95, 20.4) * mm, v(35.6, 22.24) * mm, v(35.14, 23.7) * mm, v(34.4, 26.1) * mm, v(32.3, 28.11) * mm, v(28.35, 29.49) * mm, v(26.6, 29.67) * mm, v(23.2, 29.67) * mm, v(21.74, 29.21) * mm, v(21, 28.57) * mm]});
            skFitSpline(sketch, "E26", {"points": [v(-77.73, 15.52) * mm, v(-78.18, 12.17) * mm, v(-78.4, 8.6) * mm, v(-79.74, 6.15) * mm, v(-79.52, 2.8) * mm, v(-79.07, 0) * mm, v(-78.85, -5.23) * mm, v(-78.4, -10.14) * mm, v(-77.95, -14.37) * mm, v(-76.62, -19.06) * mm, v(-75.72, -22.85) * mm, v(-73.94, -27.09) * mm, v(-71.93, -33.11) * mm, v(-71.48, -36.68) * mm, v(-70.37, -40.25) * mm, v(-67.25, -44.71) * mm, v(-65.02, -46.05) * mm, v(-60.55, -50.96) * mm, v(-60.33, -51.4) * mm, v(-56.76, -53.86) * mm, v(-54.3, -57.43) * mm, v(-49.4, -60.77) * mm, v(-44.05, -63.45) * mm, v(-41.6, -64.12) * mm, v(-35.8, -66.35) * mm, v(-27.81, -67.47) * mm, v(-23.52, -68.13) * mm, v(-18.33, -69.03) * mm, v(-11.26, -69.25) * mm, v(-5.23, -68.58) * mm, v(0, -66.73) * mm, v(5.25, -66.73) * mm, v(10.83, -66.73) * mm, v(13.97, -65.05) * mm, v(16.52, -64.24) * mm, v(17.84, -63.13) * mm, v(20.3, -63.13) * mm, v(22.5, -61.7) * mm, v(24.08, -60.81) * mm, v(25.92, -59.93) * mm, v(28.2, -59.85) * mm, v(29.8, -57.47) * mm, v(32.16, -56.5) * mm, v(33.57, -54.48) * mm, v(35.49, -52.81) * mm, v(36.96, -51.64) * mm, v(38.33, -50.46) * mm, v(40.59, -48.8) * mm, v(41.57, -47.32) * mm, v(42.84, -45.56) * mm, v(43.23, -44.48) * mm, v(44.6, -44.18) * mm, v(45.4, -42.61) * mm, v(47.55, -39.28) * mm, v(47.55, -38.5) * mm, v(48.92, -36.43) * mm, v(48.92, -35.26) * mm, v(48.24, -34.87) * mm, v(48.83, -33.4) * mm, v(50.79, -30.35) * mm, v(50.79, -28.88) * mm, v(50.79, -26.33) * mm, v(52.16, -24.57) * mm, v(53.53, -21.72) * mm, v(54.9, -17.9) * mm, v(55.6, -15.15) * mm, v(57.1, -3.86) * mm, v(57.1, 0) * mm, v(57.4, 2.24) * mm, v(57.4, 8.04) * mm, v(57.25, 12.83) * mm, v(55.07, 17.61) * mm, v(55.07, 20.08) * mm, v(54.06, 22.25) * mm, v(53.77, 25.6) * mm, v(52.32, 29.36) * mm, v(50.72, 31.97) * mm, v(51.01, 34.58) * mm, v(48.25, 35.02) * mm, v(46.93, 37.06) * mm, v(45.9, 41.05) * mm, v(44.42, 41.33) * mm, v(41.91, 44.03) * mm, v(39.84, 46.35) * mm, v(37.74, 47) * mm, v(35.79, 50.34) * mm, v(33.1, 52.1) * mm, v(30.77, 54.8) * mm, v(27.99, 55.91) * mm, v(25.02, 56.93) * mm, v(21.3, 58.88) * mm, v(18.05, 61.1) * mm, v(13.6, 62.41) * mm, v(9.81, 63.58) * mm, v(7.06, 65.76) * mm, v(5.54, 65.1) * mm, v(0.81, 65) * mm, v(-2.4, 65.2) * mm, v(-6.48, 65.48) * mm, v(-10.27, 66.14) * mm, v(-13.12, 67.37) * mm, v(-15.1, 67.47) * mm, v(-15.3, 68.88) * mm, v(-19.37, 68.88) * mm, v(-23.54, 68.13) * mm, v(-25.53, 63.96) * mm, v(-27.81, 63.87) * mm, v(-30.26, 63.87) * mm, v(-32.06, 62.41) * mm, v(-34.9, 62.41) * mm, v(-37.46, 62.41) * mm, v(-38.63, 61.01) * mm, v(-39.55, 61.01) * mm, v(-42.58, 59.22) * mm, v(-43.53, 58.75) * mm, v(-45.32, 58.23) * mm, v(-47.24, 56.61) * mm, v(-48.76, 55.6) * mm, v(-50.38, 55.3) * mm, v(-52.7, 53.07) * mm, v(-56.14, 50.04) * mm, v(-57.66, 48.02) * mm, v(-59.48, 46.2) * mm, v(-61.5, 44.38) * mm, v(-61.8, 42.3) * mm, v(-64.63, 41.66) * mm, v(-65.44, 38.92) * mm, v(-67.77, 37) * mm, v(-70.3, 32.25) * mm, v(-72.52, 28.9) * mm, v(-73.94, 26.68) * mm, v(-75.25, 22.94) * mm, v(-76.67, 18.5) * mm, v(-77.73, 15.52) * mm]});
            skSolve(sketch);
        }
        {
            var Q0;
            Q0 = qSketchRegion(id + "F0", true);
            extrude(context, id + "F1", {"entities" : qUnion([Q0]), "depth" : 25.4 * mm});
        }
    });
